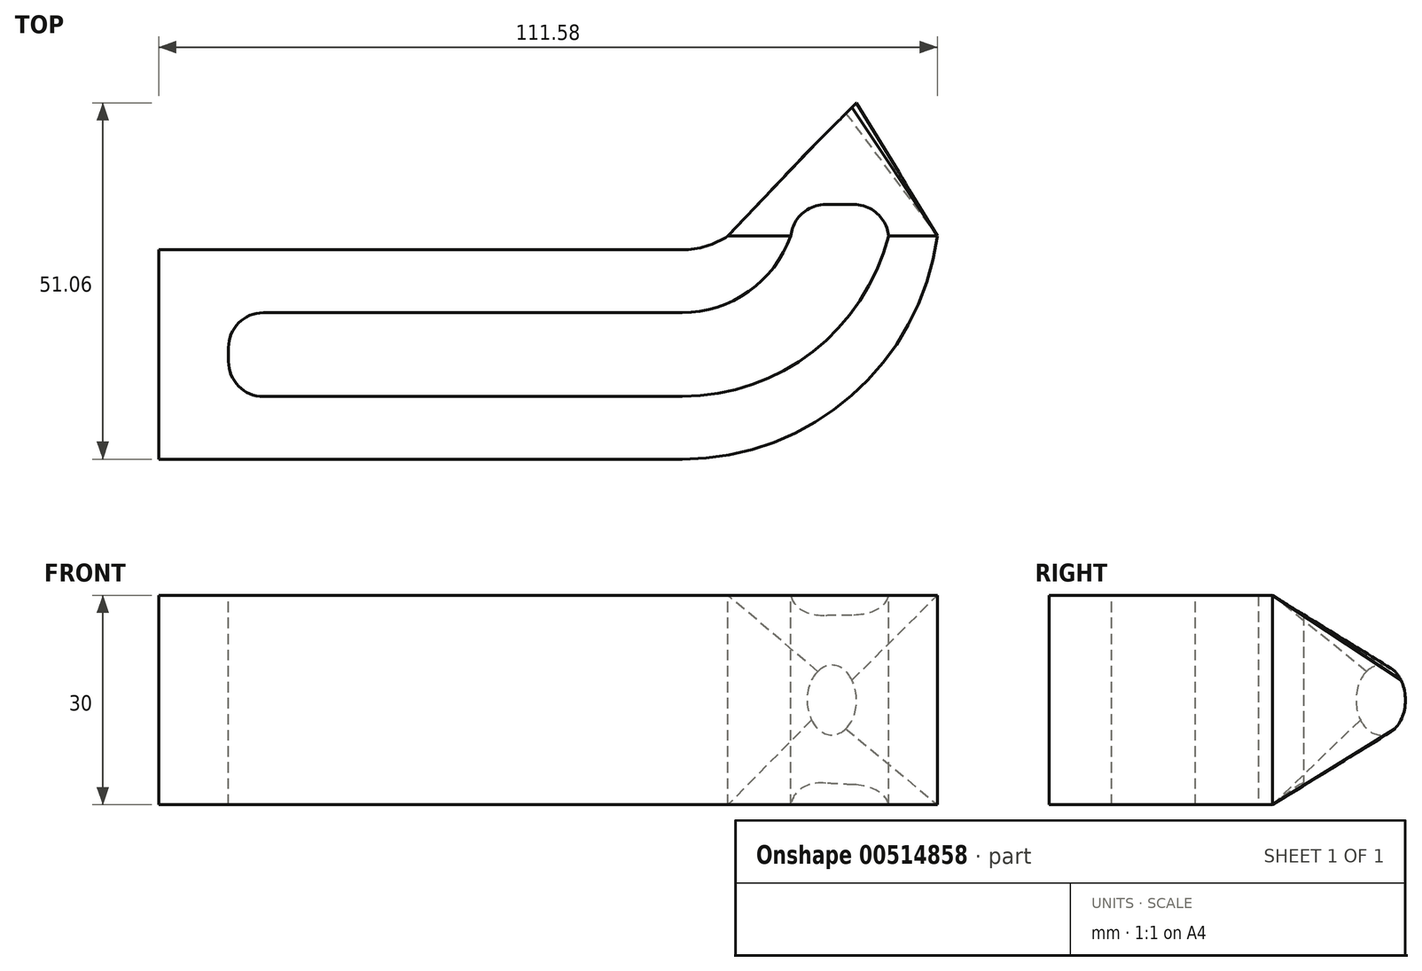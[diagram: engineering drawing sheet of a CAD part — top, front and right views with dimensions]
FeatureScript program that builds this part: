
annotation { "Feature Type Name" : "Feature", "Feature Type Description" : "" }
export const myFeature = defineFeature(function(context is Context, id is Id, definition is map)
    precondition{}
    {
        {
            var Q0;
            Q0=qCreatedBy(makeId("Top.planeOp"),FACE);
            var sketch = newSketch(context, id + "F0", { "sketchPlane" : qUnion([Q0])});
            skLineSegment(sketch, "E0.left", {"start": v(-50, 50) * mm, "end": v(-50, -50) * mm});
            skPoint(sketch, "E0.middle", {"position": v(0, 0) * mm});
            skLineSegment(sketch, "E1", {"start": v(-50, 50) * mm, "end": v(-50, 40) * mm});
            skLineSegment(sketch, "E2", {"start": v(50, 40.02) * mm, "end": v(42.93, 32.95) * mm});
            skPoint(sketch, "E3", {"position": v(-50, 0) * mm});
            skLineSegment(sketch, "E4", {"start": v(42.93, 20.95) * mm, "end": v(46.58, 20.95) * mm});
            skLineSegment(sketch, "E5", {"start": v(42.93, 20.95) * mm, "end": v(-50, 20.95) * mm});
            skLineSegment(sketch, "E6", {"start": v(-50, 40) * mm, "end": v(50, 40.02) * mm});
            skLineSegment(sketch, "E7", {"start": v(-50, 20.95) * mm, "end": v(-50, 18.95) * mm});
            skLineSegment(sketch, "E8", {"start": v(42.93, 20.95) * mm, "end": v(42.93, 32.95) * mm});
            skLineSegment(sketch, "E9", {"start": v(46.46, 36.48) * mm, "end": v(46.58, 20.95) * mm});
            skLineSegment(sketch, "E10", {"start": v(46.58, 20.95) * mm, "end": v(31.58, 20.95) * mm});
            skLineSegment(sketch, "E11", {"start": v(-50, 18.95) * mm, "end": v(25, 18.95) * mm});
            skLineSegment(sketch, "E12", {"start": v(-50, 18.95) * mm, "end": v(-50, 3.95) * mm});
            skSolve(sketch);
        }
        {
            var Q0;
            Q0=sQuery(id+"F0.wireOp",EDGE,"E2");
            cPlane(context, id + "F1", {"entities" : qUnion([Q0]), "cplaneType" : CPlaneType.LINE_ANGLE, "offset" : 25 * mm, "angle" : 90 * degree, "width" : 150 * mm, "height" : 150 * mm});
        }
        {
            var Q0;
            Q0=qCreatedBy(id+"F1.planeOp",FACE);
            var sketch = newSketch(context, id + "F2", { "sketchPlane" : qUnion([Q0])});
            skCircle(sketch, "E13", {"center": v(58.64, 0) * mm, "radius": 5 * mm});
            skSolve(sketch);
        }
        {
            var Q0;
            Q0=qCreatedBy(makeId("Front.planeOp"),FACE);
            var Q1;
            Q1=sQuery(id+"F0.wireOp",VERTEX,"E4.start");
            cPlane(context, id + "F3", {"entities" : qUnion([Q0, Q1]), "cplaneType" : CPlaneType.PLANE_POINT, "offset" : 25 * mm, "width" : 150 * mm, "height" : 150 * mm});
        }
        {
            var Q0;
            Q0=qCreatedBy(id+"F3.planeOp",FACE);
            var sketch = newSketch(context, id + "F4", { "sketchPlane" : qUnion([Q0])});
            skPoint(sketch, "E14", {"position": v(42.93, 0) * mm});
            skPoint(sketch, "E15", {"position": v(46.58, 0) * mm});
            skLineSegment(sketch, "E16.bottom", {"start": v(31.58, -15) * mm, "end": v(61.58, -15) * mm});
            skLineSegment(sketch, "E16.top", {"start": v(31.58, 15) * mm, "end": v(61.58, 15) * mm});
            skLineSegment(sketch, "E16.left", {"start": v(31.58, -15) * mm, "end": v(31.58, 15) * mm});
            skLineSegment(sketch, "E16.right", {"start": v(61.58, -15) * mm, "end": v(61.58, 15) * mm});
            skLineSegment(sketch, "E17", {"start": v(46.58, 0) * mm, "end": v(61.58, 0) * mm});
            skSolve(sketch);
        }
        {
            var Q0;
            Q0=makeQuery(id+"F2.imprint","IMPRINT",FACE,{"disambiguationData":[TD([[makeQuery(id+"F2.imprint","IMPRINT",EDGE,{"derivedFrom":sQuery(id+"F2.wireOp",EDGE,"E13")}),1.0]])]});
            var Q1;
            Q1=makeQuery(id+"F4.imprint","IMPRINT",FACE,{"disambiguationData":[TD([[makeQuery(id+"F4.imprint","IMPRINT",EDGE,{"derivedFrom":sQuery(id+"F4.wireOp",EDGE,"E16.bottom")}),1.0]])]});
            loft(context, id + "F5", {"sheetProfilesArray" : [{ "sheetProfileEntities" : qUnion([Q0]) }, { "sheetProfileEntities" : qUnion([Q1]) }]});
        }
        {
            var Q0;
            Q0=sQuery(id+"F0.wireOp",VERTEX,"E11.end");
            var Q1;
            Q1=qCreatedBy(makeId("Right.planeOp"),FACE);
            cPlane(context, id + "F6", {"entities" : qUnion([Q0, Q1]), "cplaneType" : CPlaneType.PLANE_POINT, "offset" : 25 * mm, "width" : 150 * mm, "height" : 150 * mm});
        }
        {
            var Q0;
            Q0=qCreatedBy(id+"F6.planeOp",FACE);
            var sketch = newSketch(context, id + "F7", { "sketchPlane" : qUnion([Q0])});
            skPoint(sketch, "E18", {"position": v(18.95, 0) * mm});
            skLineSegment(sketch, "E19.bottom", {"start": v(18.95, 15) * mm, "end": v(-11.05, 15) * mm});
            skLineSegment(sketch, "E19.top", {"start": v(18.95, -15) * mm, "end": v(-11.05, -15) * mm});
            skLineSegment(sketch, "E19.left", {"start": v(18.95, 15) * mm, "end": v(18.95, -15) * mm});
            skLineSegment(sketch, "E19.right", {"start": v(-11.05, 15) * mm, "end": v(-11.05, -15) * mm});
            skPoint(sketch, "E19.middle", {"position": v(3.95, 0) * mm});
            skLineSegment(sketch, "E20", {"start": v(3.95, 0) * mm, "end": v(3.95, 15) * mm});
            skSolve(sketch);
        }
        {
            var Q0;
            Q0=sQuery(id+"F7.wireOp",VERTEX,"E19.middle");
            var Q1;
            Q1=qCreatedBy(makeId("Top.planeOp"),FACE);
            cPlane(context, id + "F8", {"entities" : qUnion([Q0, Q1]), "cplaneType" : CPlaneType.PLANE_POINT, "offset" : 25 * mm, "width" : 150 * mm, "height" : 150 * mm});
        }
        {
            var Q0;
            Q0=qCreatedBy(id+"F8.planeOp",FACE);
            var sketch = newSketch(context, id + "F9", { "sketchPlane" : qUnion([Q0])});
            skPoint(sketch, "E21", {"position": v(25, -11.05) * mm});
            skPoint(sketch, "E22", {"position": v(25, 18.95) * mm});
            skLineSegment(sketch, "E23", {"start": v(25, 18.95) * mm, "end": v(17.07, 18.95) * mm});
            skLineSegment(sketch, "E24", {"start": v(25, -11.05) * mm, "end": v(17.63, -11.05) * mm});
            skPoint(sketch, "E25", {"position": v(31.58, 20.95) * mm});
            skPoint(sketch, "E26", {"position": v(61.58, 20.95) * mm});
            skArc(sketch, "E27", {"start": v(25, 18.95) * mm, "mid": v(28.44, 19.46) * mm, "end": v(31.58, 20.95) * mm});
            skArc(sketch, "E28", {"start": v(25, -11.05) * mm, "mid": v(49.3, -1.92) * mm, "end": v(61.58, 20.95) * mm});
            skLineSegment(sketch, "E29", {"start": v(25, 18.95) * mm, "end": v(25, -11.05) * mm});
            skLineSegment(sketch, "E30", {"start": v(31.58, 20.95) * mm, "end": v(61.58, 20.95) * mm});
            skSolve(sketch);
        }
        {
            var Q0;
            Q0=makeQuery(id+"F9.imprint","IMPRINT",FACE,{"disambiguationData":[TD([[makeQuery(id+"F9.imprint","IMPRINT",EDGE,{"derivedFrom":sQuery(id+"F9.wireOp",EDGE,"E27")}),-1.0]])]});
            extrude(context, id + "F10", {"entities" : qUnion([Q0]), "operationType" : NewBodyOperationType.ADD, "endBound" : BoundingType.SYMMETRIC, "depth" : 30 * mm, "offsetDistance" : 25 * mm});
        }
        {
            var Q0;
            Q0=qCreatedBy(makeId("Top.planeOp"),FACE);
            var sketch = newSketch(context, id + "F11", { "sketchPlane" : qUnion([Q0])});
            skPoint(sketch, "E31", {"position": v(25, 3.95) * mm});
            skPoint(sketch, "E32", {"position": v(-50, 3.95) * mm});
            skLineSegment(sketch, "E33", {"start": v(-50, 3.95) * mm, "end": v(25, 3.95) * mm});
            skSolve(sketch);
        }
        {
            var Q0;
            {var subQ1=sQuery(id+"F7.wireOp",EDGE,"E19.bottom");Q0=makeQuery(id+"F7.imprint","IMPRINT",FACE,{"disambiguationData":[TD([[makeQuery(id+"F7.imprint","IMPRINT",EDGE,{"derivedFrom":subQ1}),1.0]])]});}
            var Q1;
            Q1=sQuery(id+"F11.wireOp",EDGE,"E33");
            sweep(context, id + "F12", {"operationType" : NewBodyOperationType.ADD, "profiles" : qUnion([Q0]), "path" : qUnion([Q1])});
        }
        {
            var Q0;
            Q0=makeQuery(id+"F12.boolean.opBoolean","MERGE",FACE,{"derivedFrom":[makeQuery(id+"F10.opExtrude","CAP_FACE",FACE,{"disambiguationData":[OSD([sQuery(id+"F9.wireOp",EDGE,"E27"),sQuery(id+"F9.wireOp",EDGE,"E28"),sQuery(id+"F9.wireOp",EDGE,"E29"),sQuery(id+"F9.wireOp",EDGE,"E30")])],"isStart":false}),makeQuery(id+"F12.opSweep","SWEPT_FACE",FACE,{"disambiguationData":[OSD([sQuery(id+"F7.wireOp",EDGE,"E19.bottom"),sQuery(id+"F11.wireOp",EDGE,"E33")])]})]});
            var sketch = newSketch(context, id + "F13", { "sketchPlane" : qUnion([Q0])});
            skPoint(sketch, "E34", {"position": v(25, 3.95) * mm});
            skPoint(sketch, "E35", {"position": v(31.58, 20.95) * mm});
            skPoint(sketch, "E36", {"position": v(61.58, 20.95) * mm});
            skLineSegment(sketch, "E37", {"start": v(31.58, 20.95) * mm, "end": v(31.58, 13.45) * mm});
            skPoint(sketch, "E38", {"position": v(25, -11.05) * mm});
            skLineSegment(sketch, "E39", {"start": v(25, 9.95) * mm, "end": v(-40, 9.95) * mm});
            skLineSegment(sketch, "E40", {"start": v(25, -2.05) * mm, "end": v(-40, -2.05) * mm});
            skLineSegment(sketch, "E41", {"start": v(-40, 9.95) * mm, "end": v(-40, -2.05) * mm});
            skArc(sketch, "E42", {"start": v(25, 9.95) * mm, "mid": v(34.54, 12.98) * mm, "end": v(40.58, 20.95) * mm});
            skLineSegment(sketch, "E43", {"start": v(40.58, 20.95) * mm, "end": v(54.58, 20.95) * mm});
            skArc(sketch, "E44", {"start": v(25, -2.05) * mm, "mid": v(43.74, 4.37) * mm, "end": v(54.58, 20.95) * mm});
            skLineSegment(sketch, "E45", {"start": v(40.58, 20.95) * mm, "end": v(40.58, 25.45) * mm});
            skLineSegment(sketch, "E46", {"start": v(40.58, 25.45) * mm, "end": v(54.58, 25.45) * mm});
            skLineSegment(sketch, "E47", {"start": v(54.58, 25.45) * mm, "end": v(54.58, 20.95) * mm});
            skSolve(sketch);
        }
        {
            var Q0;
            Q0=makeQuery(id+"F13.imprint","IMPRINT",FACE,{"disambiguationData":[TD([[makeQuery(id+"F13.imprint","IMPRINT",EDGE,{"derivedFrom":sQuery(id+"F13.wireOp",EDGE,"E39")}),1.0]])]});
            var Q1;
            Q1=makeQuery(id+"F13.imprint","IMPRINT",FACE,{"disambiguationData":[TD([[makeQuery(id+"F13.imprint","IMPRINT",EDGE,{"derivedFrom":sQuery(id+"F13.wireOp",EDGE,"E43")}),-1.0]])]});
            extrude(context, id + "F14", {"entities" : qUnion([Q0, Q1]), "operationType" : NewBodyOperationType.REMOVE, "oppositeDirection" : true, "depth" : 30 * mm, "offsetDistance" : 25 * mm});
        }
        {
            var Q0;
            Q0=makeQuery(id+"F14.boolean.opBoolean","COPY",EDGE,{"derivedFrom":makeQuery(id+"F14.opExtrude","SWEPT_EDGE",EDGE,{"disambiguationData":[OSD([sQuery(id+"F13.wireOp",EDGE,"E39"),sQuery(id+"F13.wireOp",EDGE,"E41")])]})});
            var Q1;
            Q1=makeQuery(id+"F14.boolean.opBoolean","COPY",EDGE,{"derivedFrom":makeQuery(id+"F14.opExtrude","SWEPT_EDGE",EDGE,{"disambiguationData":[OSD([sQuery(id+"F13.wireOp",EDGE,"E40"),sQuery(id+"F13.wireOp",EDGE,"E41")])]})});
            var Q2;
            Q2=makeQuery(id+"F14.boolean.opBoolean","COPY",EDGE,{"derivedFrom":makeQuery(id+"F14.opExtrude","SWEPT_EDGE",EDGE,{"disambiguationData":[OSD([sQuery(id+"F13.wireOp",EDGE,"E45"),sQuery(id+"F13.wireOp",EDGE,"E46")])]})});
            var Q3;
            Q3=makeQuery(id+"F14.boolean.opBoolean","COPY",EDGE,{"derivedFrom":makeQuery(id+"F14.opExtrude","SWEPT_EDGE",EDGE,{"disambiguationData":[OSD([sQuery(id+"F13.wireOp",EDGE,"E47"),sQuery(id+"F13.wireOp",EDGE,"E46")])]})});
            fillet(context, id + "F15", {"entities" : qUnion([Q0, Q1, Q2, Q3]), "radius" : 5 * mm, "tangentPropagation" : true, "allowEdgeOverflow" : false});
        }
    });
